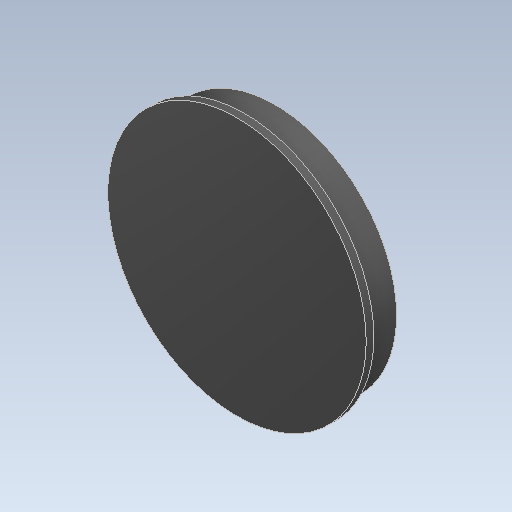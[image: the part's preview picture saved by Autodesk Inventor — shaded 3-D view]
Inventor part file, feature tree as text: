
AUTODESK INVENTOR PART (.ipt)
format: ipt  version: 2021 (Build 250183000, 183)  size: 104,448 bytes
history: native  units: mm
features: other x1, revolve x1
ambient origin geometry x8: Origin, YZ Plane, XZ Plane, XY Plane, X Axis, Y Axis, Z Axis, Center Point
bodies: Body1 (feature_tree)
feature tree (2):
  other  "Sólido1"
  revolve  "Revolve1"  [1 undecoded]
note: 1 required parameter value undecoded (feature->parameter linkage not recoverable at this tier; creation-order binding heuristic only, values carry confidence <= 0.55)
